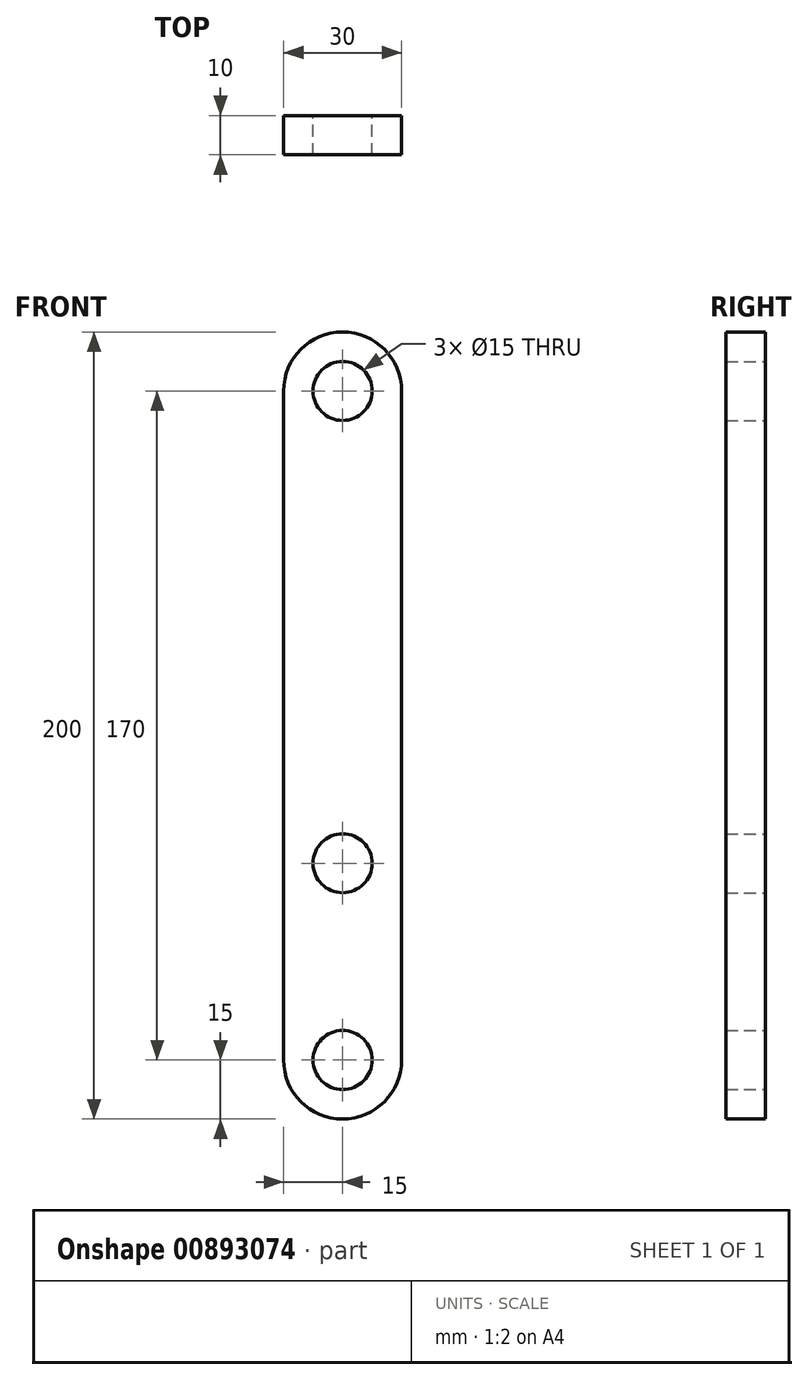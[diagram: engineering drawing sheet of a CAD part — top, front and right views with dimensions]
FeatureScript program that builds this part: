
annotation { "Feature Type Name" : "Feature", "Feature Type Description" : "" }
export const myFeature = defineFeature(function(context is Context, id is Id, definition is map)
    precondition{}
    {
        {
            var Q0;
            Q0=qCreatedBy(makeId("Front.planeOp"),FACE);
            var sketch = newSketch(context, id + "F0", { "sketchPlane" : qUnion([Q0])});
            skArc(sketch, "E0", {"start": v(15, 85) * mm, "mid": v(0, 100) * mm, "end": v(-15, 85) * mm});
            skArc(sketch, "E1", {"start": v(-15, -85) * mm, "mid": v(0, -100) * mm, "end": v(15, -85) * mm});
            skLineSegment(sketch, "E2", {"start": v(-15, 85) * mm, "end": v(-15, -85) * mm});
            skLineSegment(sketch, "E3", {"start": v(15, 85) * mm, "end": v(15, -85) * mm});
            skSolve(sketch);
        }
        {
            var Q0;
            Q0 = qSketchRegion(id + "F0", true);
            extrude(context, id + "F1", {"entities" : qUnion([Q0]), "depth" : 10 * mm, "offsetDistance" : 25 * mm});
        }
        {
            var Q0;
            Q0=qCreatedBy(makeId("Front.planeOp"),FACE);
            var sketch = newSketch(context, id + "F2", { "sketchPlane" : qUnion([Q0])});
            skCircle(sketch, "E4", {"center": v(0, 85) * mm, "radius": 7.5 * mm});
            skCircle(sketch, "E5", {"center": v(0, -35) * mm, "radius": 7.5 * mm});
            skCircle(sketch, "E6", {"center": v(0, -85) * mm, "radius": 7.5 * mm});
            skSolve(sketch);
        }
        {
            var Q0;
            Q0 = qSketchRegion(id + "F2", true);
            extrude(context, id + "F3", {"entities" : qUnion([Q0]), "operationType" : NewBodyOperationType.REMOVE, "depth" : 51 * mm, "offsetDistance" : 25 * mm});
        }
    });
